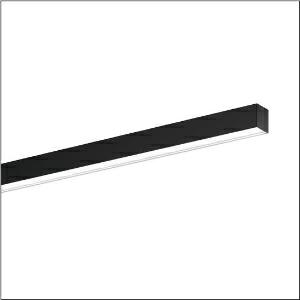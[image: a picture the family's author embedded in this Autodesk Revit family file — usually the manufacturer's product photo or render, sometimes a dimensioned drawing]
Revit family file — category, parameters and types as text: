
# Revit family: silica_r__21_51mx20db42bb_5dab
name_source: partatom
category: Lighting Fixtures
units: mm (PartAtom-declared; Revit-internal decimal feet)

## family parameters
Cut with Voids When Loaded = No
Host = Face
Light Source = No
Part Type = Normal
Room Calculation Point = No
Round Connector Dimension = Use Diameter
Shared = No

## types (1)
- --- (1 x LED, 3000 lm, 19 W, 4000K)
    Apparent Load = 19 VA
    CIE Flux Codes = 48 79 96 100 100
    Color Rendering = 80
    Color Temperature = 4000K
    Default Elevation = 1800 mm
    Description = Silica® 21, office luminaire, primary optical cover: cover, of PMMA, opal, light emission: direct distribution, primary light characteristic: symmetric, installation type: surface-mounted, LED, rated luminous flux: 3.000lm, luminous efficacy: 158lm/W, light colour: 840, colour temperature: 4000K, with terminal, 3+2-pole, max. 2.5mm², mains connection: 220..240V, AC, 50/60Hz, rated input power: 19W, luminaire housing, of aluminium, jet black (RAL 9005), length: 1.504mm, width: 53mm, height: 53mm, protection rating (complete): IP20, insulation class (complete): insulation class I (protective earthing), certification: CE, permissible operating ambient temperature: 0..+35°C, standard: EN 50419, packaging unit: 1 piece
    Height = 0 mm  [stored 0 ft]
    Lamp = 1 x LED
    Lamp Light Flux = 3000 lm
    Lamp Power = 19 W
    Lamp count = 1
    Length = 1504 mm
    Luminous efficacy = 158 lm/W
    Manufacturer = Siteco
    ModVariant = No
    Model = 51MX20DB42BB
    Mounting Place = Ceiling
    Mounting Type = Recessed
    Number of Poles = 1
    OnlyDefault = Yes
    Power Factor = 1
    Product Name = Silica® 21
    Product group = office luminaire | ceiling recessed
    ProductGroupID = 401
    Protection Class = Protection class I
    Protection Degree = IP 20
    RLX_Detail_Level = 1
    RLX_Emergency_Light_Flux = 0 lm
    RLX_Emergency_Type = 0
    RLX_Emergency_Type_DB = No
    RlxData = <blob elided: 28677 chars, md5=7cb2bdea>
    Socket = socket
    Standby Power = 0 W
    System Light Flux = 3000 lm
    System Power = 19 W
    Type Comments = factory setting: luminous flux: 100 % | dim-lin: 254 | 218 mA
    Type Image = l_1297760.jpg
    URL = http://relux.com
    VarID = @adj_048289
    Voltage = 0 V
    Weight = 0.00 kg
    Width = 53 mm

note: [stored X ft] marks values corroborated as IEEE doubles in the binary element streams (Revit-internal decimal feet)

## geometry (parser evidence)
native form markers: Blend x4, Sweep x10
no freeform markers — native parametric forms only
